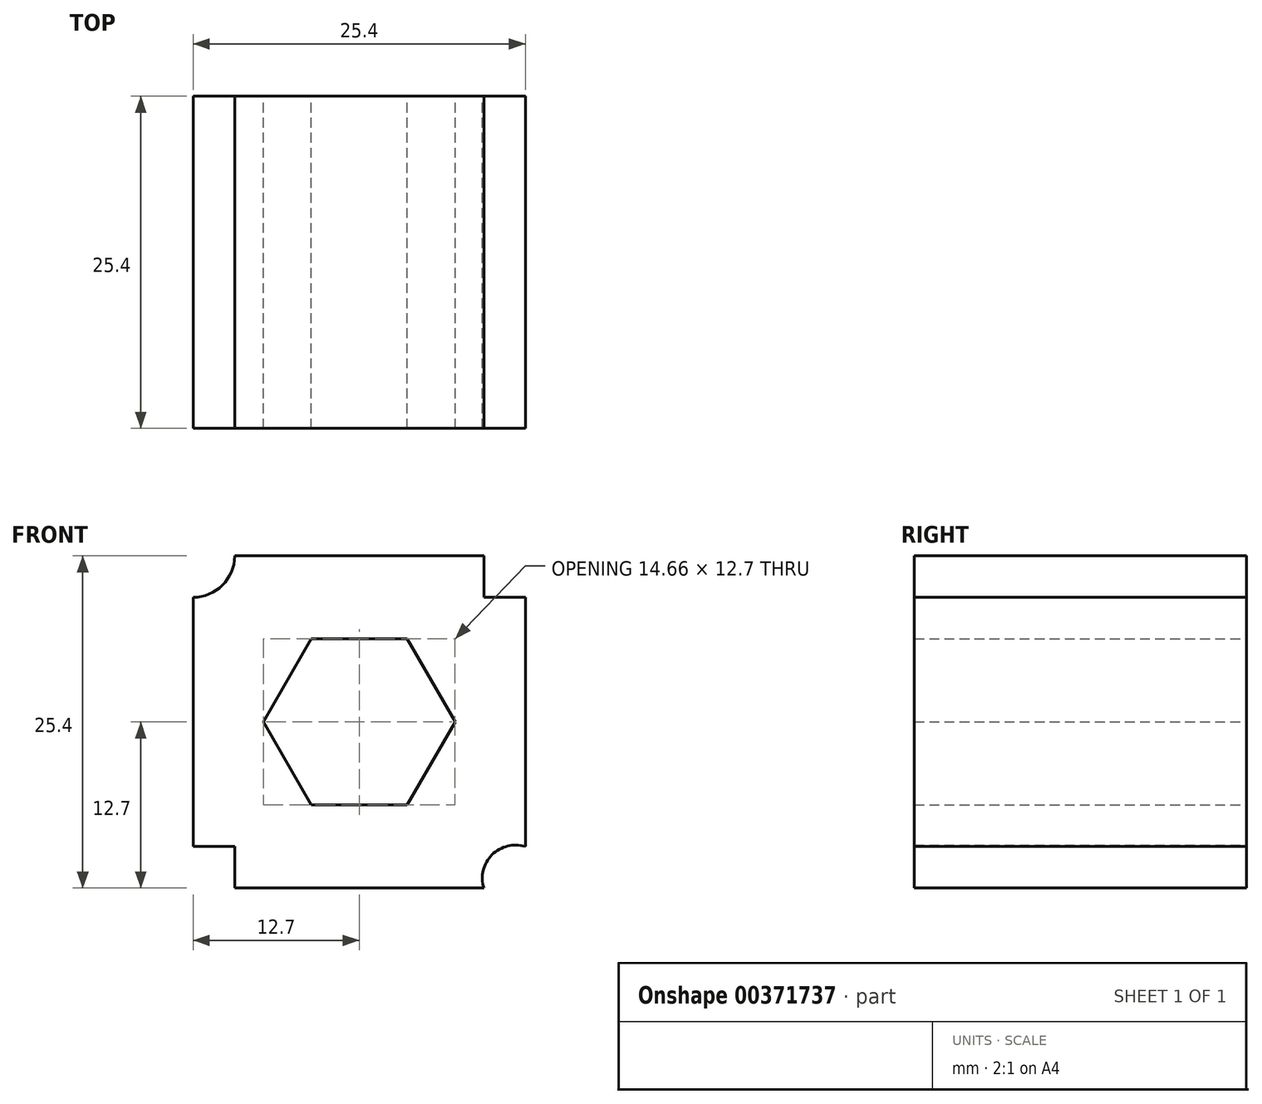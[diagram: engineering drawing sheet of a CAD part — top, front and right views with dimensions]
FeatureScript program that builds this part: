
annotation { "Feature Type Name" : "Feature", "Feature Type Description" : "" }
export const myFeature = defineFeature(function(context is Context, id is Id, definition is map)
    precondition{}
    {
        {
            var Q0;
            Q0=qCreatedBy(makeId("Front.planeOp"),FACE);
            var sketch = newSketch(context, id + "F0", { "sketchPlane" : qUnion([Q0])});
            skLineSegment(sketch, "E0.bottom", {"start": v(9.52, 12.7) * mm, "end": v(-9.53, 12.7) * mm});
            skLineSegment(sketch, "E0.top", {"start": v(9.53, -12.7) * mm, "end": v(-9.52, -12.7) * mm});
            skLineSegment(sketch, "E0.left", {"start": v(12.7, 9.53) * mm, "end": v(12.7, -9.52) * mm});
            skLineSegment(sketch, "E0.right", {"start": v(-12.7, 9.53) * mm, "end": v(-12.7, -9.52) * mm});
            skPoint(sketch, "E0.middle", {"position": v(0, 0) * mm});
            skCircle(sketch, "E1.cCircle", {"center": v(0, 0) * mm, "radius": 6.35 * mm, "construction": true});
            skLineSegment(sketch, "E1.0", {"start": v(3.67, 6.35) * mm, "end": v(7.33, 0) * mm});
            skLineSegment(sketch, "E1.1", {"start": v(7.33, 0) * mm, "end": v(3.67, -6.35) * mm});
            skLineSegment(sketch, "E1.2", {"start": v(3.67, -6.35) * mm, "end": v(-3.67, -6.35) * mm});
            skLineSegment(sketch, "E1.3", {"start": v(-3.67, -6.35) * mm, "end": v(-7.33, 0) * mm});
            skLineSegment(sketch, "E1.4", {"start": v(-7.33, 0) * mm, "end": v(-3.67, 6.35) * mm});
            skLineSegment(sketch, "E1.5", {"start": v(-3.67, 6.35) * mm, "end": v(3.67, 6.35) * mm});
            skPoint(sketch, "E1.0.midPoint", {"position": v(5.5, 3.18) * mm});
            skArc(sketch, "E2", {"start": v(-12.7, 9.53) * mm, "mid": v(-10.45, 10.45) * mm, "end": v(-9.53, 12.7) * mm});
            skLineSegment(sketch, "E3.top", {"start": v(12.7, 9.53) * mm, "end": v(9.52, 9.53) * mm});
            skLineSegment(sketch, "E3.right", {"start": v(9.52, 12.7) * mm, "end": v(9.52, 9.53) * mm});
            skPoint(sketch, "E4.orphan", {"position": v(12.7, 12.7) * mm});
            skLineSegment(sketch, "E5.top", {"start": v(-12.7, -9.52) * mm, "end": v(-9.52, -9.52) * mm});
            skLineSegment(sketch, "E5.right", {"start": v(-9.52, -12.7) * mm, "end": v(-9.52, -9.52) * mm});
            skPoint(sketch, "E5.bottom.start.orphan", {"position": v(-12.7, -12.7) * mm});
            skArc(sketch, "E6", {"start": v(12.7, -9.52) * mm, "mid": v(10.16, -10.16) * mm, "end": v(9.53, -12.7) * mm});
            skSolve(sketch);
        }
        {
            var Q0;
            Q0 = qSketchRegion(id + "F0", true);
            extrude(context, id + "F1", {"entities" : qUnion([Q0]), "depth" : 25.4 * mm});
        }
    });
